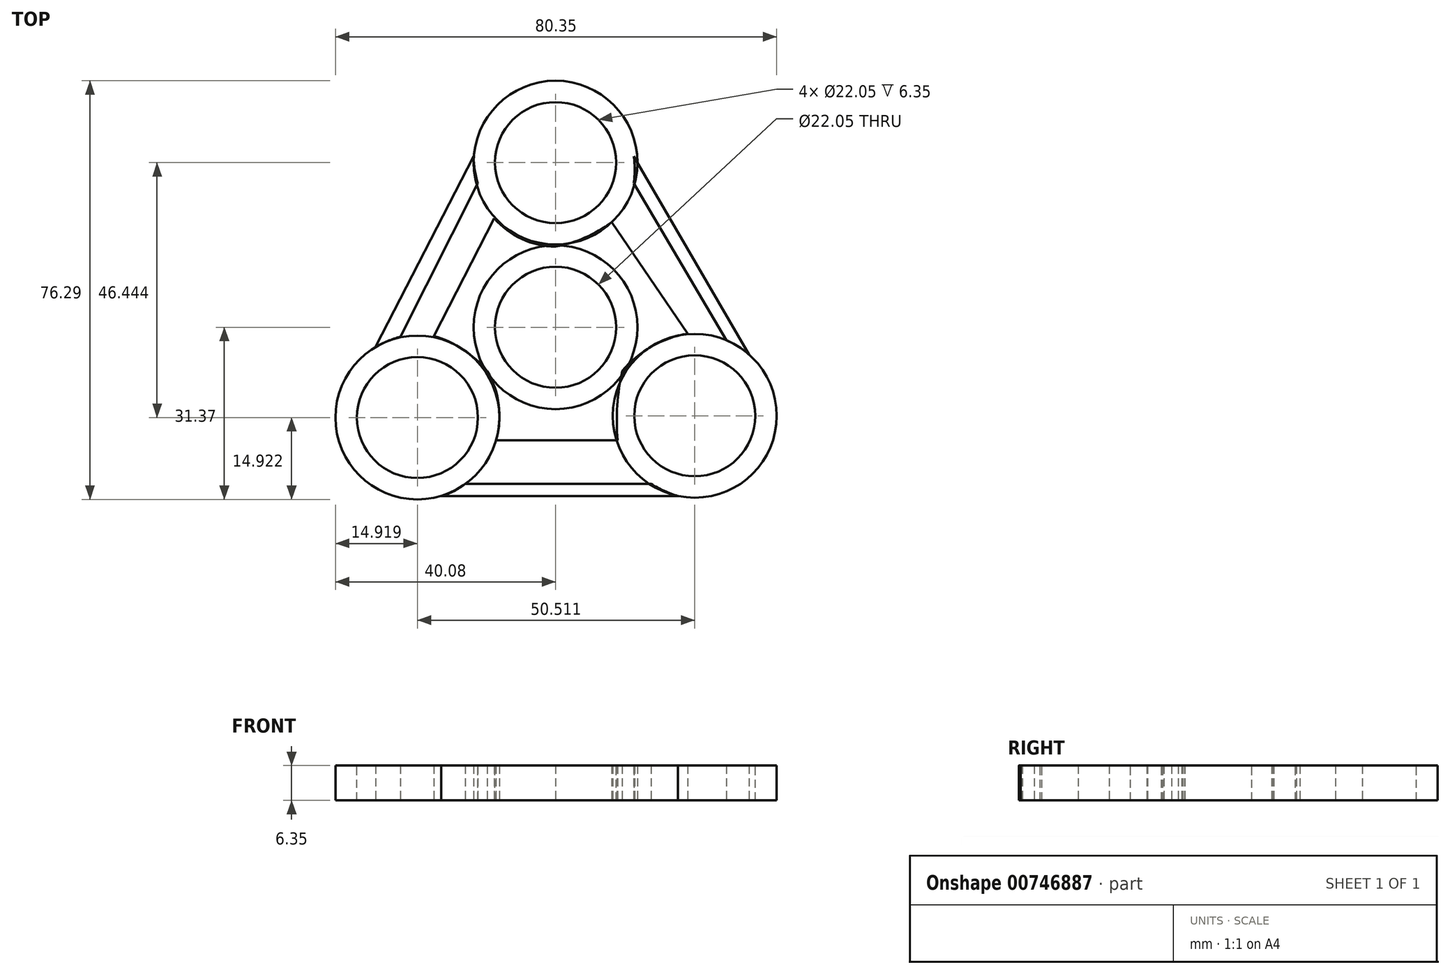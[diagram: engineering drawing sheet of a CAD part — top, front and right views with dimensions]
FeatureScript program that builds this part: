
annotation { "Feature Type Name" : "Feature", "Feature Type Description" : "" }
export const myFeature = defineFeature(function(context is Context, id is Id, definition is map)
    precondition{}
    {
        {
            var Q0;
            Q0=qCreatedBy(makeId("Top.planeOp"),FACE);
            var sketch = newSketch(context, id + "F0", { "sketchPlane" : qUnion([Q0])});
            skCircle(sketch, "E0", {"center": v(0, 0) * mm, "radius": 14.92 * mm});
            skSolve(sketch);
        }
        {
            var Q0;
            Q0 = qSketchRegion(id + "F0", true);
            extrude(context, id + "F1", {"entities" : qUnion([Q0]), "depth" : 6.35 * mm, "offsetDistance" : 25.4 * mm});
        }
        {
            var Q0;
            Q0=makeQuery(id+"F1.opExtrude","CAP_FACE",FACE,{"disambiguationData":[OSD([sQuery(id+"F0.wireOp",EDGE,"E0")])],"isStart":false});
            var sketch = newSketch(context, id + "F2", { "sketchPlane" : qUnion([Q0])});
            skCircle(sketch, "E1", {"center": v(0, 0) * mm, "radius": 11.02 * mm});
            skSolve(sketch);
        }
        {
            var Q0;
            Q0 = qSketchRegion(id + "F2", true);
            extrude(context, id + "F3", {"entities" : qUnion([Q0]), "operationType" : NewBodyOperationType.REMOVE, "oppositeDirection" : true, "depth" : 25.4 * mm, "offsetDistance" : 25.4 * mm});
        }
        {
            var Q0;
            Q0=qCreatedBy(makeId("Top.planeOp"),FACE);
            var sketch = newSketch(context, id + "F4", { "sketchPlane" : qUnion([Q0])});
            skCircle(sketch, "E2", {"center": v(0, 30) * mm, "radius": 14.92 * mm});
            skCircle(sketch, "E3", {"center": v(25.35, -16.14) * mm, "radius": 14.92 * mm});
            skCircle(sketch, "E4", {"center": v(-25.16, -16.45) * mm, "radius": 14.92 * mm});
            skSolve(sketch);
        }
        {
            var Q0;
            Q0 = qSketchRegion(id + "F4", true);
            extrude(context, id + "F5", {"entities" : qUnion([Q0]), "depth" : 6.35 * mm, "offsetDistance" : 25.4 * mm});
        }
        {
            var Q0;
            Q0=makeQuery(id+"F5.opExtrude","CAP_FACE",FACE,{"disambiguationData":[OSD([sQuery(id+"F4.wireOp",EDGE,"E2")])],"isStart":false});
            var sketch = newSketch(context, id + "F6", { "sketchPlane" : qUnion([Q0])});
            skCircle(sketch, "E5", {"center": v(-25.16, -16.45) * mm, "radius": 11.02 * mm});
            skSolve(sketch);
        }
        {
            var Q0;
            Q0 = qSketchRegion(id + "F6", true);
            extrude(context, id + "F7", {"entities" : qUnion([Q0]), "operationType" : NewBodyOperationType.REMOVE, "oppositeDirection" : true, "depth" : 25.4 * mm, "offsetDistance" : 25.4 * mm});
        }
        {
            var Q0;
            Q0=makeQuery(id+"F5.opExtrude","CAP_FACE",FACE,{"disambiguationData":[OSD([sQuery(id+"F4.wireOp",EDGE,"E3")])],"isStart":false});
            var sketch = newSketch(context, id + "F8", { "sketchPlane" : qUnion([Q0])});
            skCircle(sketch, "E6", {"center": v(25.35, -16.14) * mm, "radius": 11.02 * mm});
            skSolve(sketch);
        }
        {
            var Q0;
            Q0 = qSketchRegion(id + "F8", true);
            extrude(context, id + "F9", {"entities" : qUnion([Q0]), "operationType" : NewBodyOperationType.REMOVE, "oppositeDirection" : true, "depth" : 25.4 * mm, "offsetDistance" : 25.4 * mm});
        }
        {
            var Q0;
            Q0=makeQuery(id+"F5.opExtrude","CAP_FACE",FACE,{"disambiguationData":[OSD([sQuery(id+"F4.wireOp",EDGE,"E2")])],"isStart":false});
            var sketch = newSketch(context, id + "F10", { "sketchPlane" : qUnion([Q0])});
            skCircle(sketch, "E7", {"center": v(0, 30) * mm, "radius": 11.02 * mm});
            skSolve(sketch);
        }
        {
            var Q0;
            Q0 = qSketchRegion(id + "F10", true);
            extrude(context, id + "F11", {"entities" : qUnion([Q0]), "operationType" : NewBodyOperationType.REMOVE, "oppositeDirection" : true, "depth" : 25.4 * mm, "offsetDistance" : 25.4 * mm});
        }
        {
            var Q0;
            Q0=qCreatedBy(makeId("Top.planeOp"),FACE);
            var sketch = newSketch(context, id + "F12", { "sketchPlane" : qUnion([Q0])});
            skLineSegment(sketch, "E8", {"start": v(14.24, 26.27) * mm, "end": v(31.1, -2.37) * mm});
            skLineSegment(sketch, "E9", {"start": v(35.24, -4.98) * mm, "end": v(14.24, 31.17) * mm});
            skArc(sketch, "E10", {"start": v(14.24, 26.27) * mm, "mid": v(14.43, 28.72) * mm, "end": v(14.24, 31.17) * mm});
            skArc(sketch, "E11", {"start": v(35.24, -4.98) * mm, "mid": v(33.27, -3.5) * mm, "end": v(31.1, -2.37) * mm});
            skLineSegment(sketch, "E12", {"start": v(-20.8, -30.75) * mm, "end": v(22.32, -30.75) * mm});
            skLineSegment(sketch, "E13", {"start": v(17.42, -28.55) * mm, "end": v(-16.42, -28.55) * mm});
            skArc(sketch, "E14", {"start": v(-20.8, -30.75) * mm, "mid": v(-18.5, -29.86) * mm, "end": v(-16.42, -28.55) * mm});
            skArc(sketch, "E15", {"start": v(17.42, -28.55) * mm, "mid": v(19.8, -29.82) * mm, "end": v(22.32, -30.75) * mm});
            skLineSegment(sketch, "E16", {"start": v(-14.94, 31.17) * mm, "end": v(-32.78, -3.53) * mm});
            skLineSegment(sketch, "E17", {"start": v(-14.18, 26.27) * mm, "end": v(-28.23, -1.73) * mm});
            skArc(sketch, "E18", {"start": v(-14.94, 31.17) * mm, "mid": v(-14.74, 28.7) * mm, "end": v(-14.18, 26.27) * mm});
            skArc(sketch, "E19", {"start": v(-28.23, -1.73) * mm, "mid": v(-30.56, -2.5) * mm, "end": v(-32.78, -3.53) * mm});
            skSolve(sketch);
        }
        {
            var Q0;
            Q0=makeQuery(id+"F12.imprint","IMPRINT",FACE,{"disambiguationData":[TD([[makeQuery(id+"F12.imprint","IMPRINT",EDGE,{"derivedFrom":sQuery(id+"F12.wireOp",EDGE,"E16")}),1.0]])]});
            var Q1;
            Q1=makeQuery(id+"F12.imprint","IMPRINT",FACE,{"disambiguationData":[TD([[makeQuery(id+"F12.imprint","IMPRINT",EDGE,{"derivedFrom":sQuery(id+"F12.wireOp",EDGE,"E8")}),1.0]])]});
            var Q2;
            Q2=makeQuery(id+"F12.imprint","IMPRINT",FACE,{"disambiguationData":[TD([[makeQuery(id+"F12.imprint","IMPRINT",EDGE,{"derivedFrom":sQuery(id+"F12.wireOp",EDGE,"E12")}),1.0]])]});
            extrude(context, id + "F13", {"entities" : qUnion([Q0, Q1, Q2]), "depth" : 6.35 * mm, "offsetDistance" : 25.4 * mm});
        }
        {
            var Q0;
            Q0=qCreatedBy(makeId("Top.planeOp"),FACE);
            var sketch = newSketch(context, id + "F14", { "sketchPlane" : qUnion([Q0])});
            skLineSegment(sketch, "E20", {"start": v(10.2, 19.16) * mm, "end": v(24.08, -1.16) * mm});
            skArc(sketch, "E21", {"start": v(24.08, -1.16) * mm, "mid": v(17.52, -3.5) * mm, "end": v(12.16, -7.93) * mm});
            skArc(sketch, "E22", {"start": v(12.16, -7.93) * mm, "mid": v(12.76, 6.97) * mm, "end": v(0, 14.68) * mm});
            skArc(sketch, "E23", {"start": v(0, 14.68) * mm, "mid": v(5.36, 16.32) * mm, "end": v(10.2, 19.16) * mm});
            skLineSegment(sketch, "E24", {"start": v(-11.17, 19.83) * mm, "end": v(-22.15, -1.59) * mm});
            skArc(sketch, "E25", {"start": v(-11.17, 19.83) * mm, "mid": v(-6.14, 16.06) * mm, "end": v(0, 14.68) * mm});
            skArc(sketch, "E26", {"start": v(0, 14.68) * mm, "mid": v(-13.05, 7.06) * mm, "end": v(-12.42, -8.04) * mm});
            skArc(sketch, "E27", {"start": v(-12.42, -8.04) * mm, "mid": v(-16.8, -4.08) * mm, "end": v(-22.15, -1.59) * mm});
            skLineSegment(sketch, "E28", {"start": v(-10.84, -20.6) * mm, "end": v(11.32, -20.6) * mm});
            skArc(sketch, "E29", {"start": v(-10.84, -20.6) * mm, "mid": v(-10.34, -14.15) * mm, "end": v(-12.42, -8.04) * mm});
            skArc(sketch, "E30", {"start": v(-12.42, -8.04) * mm, "mid": v(-0.1, -14.82) * mm, "end": v(12.16, -7.93) * mm});
            skArc(sketch, "E31", {"start": v(12.16, -7.93) * mm, "mid": v(11.24, -14.23) * mm, "end": v(11.32, -20.6) * mm});
            skSolve(sketch);
        }
        {
            var Q0;
            Q0 = qSketchRegion(id + "F14", true);
            extrude(context, id + "F15", {"entities" : qUnion([Q0]), "depth" : 6.35 * mm, "offsetDistance" : 25.4 * mm});
        }
        {
            var Q0;
            Q0=makeQuery(id+"F15.opExtrude","CAP_FACE",FACE,{"disambiguationData":[OSD([sQuery(id+"F14.wireOp",EDGE,"E20"),sQuery(id+"F14.wireOp",EDGE,"E21"),sQuery(id+"F14.wireOp",EDGE,"E23"),sQuery(id+"F14.wireOp",EDGE,"E24"),sQuery(id+"F14.wireOp",EDGE,"E25"),sQuery(id+"F14.wireOp",EDGE,"E26"),sQuery(id+"F14.wireOp",EDGE,"E27"),sQuery(id+"F14.wireOp",EDGE,"E28"),sQuery(id+"F14.wireOp",EDGE,"E29"),sQuery(id+"F14.wireOp",EDGE,"E31")])],"isStart":false});
            var sketch = newSketch(context, id + "F16", { "sketchPlane" : qUnion([Q0])});
            skCircle(sketch, "E32", {"center": v(0, 0) * mm, "radius": 11.02 * mm});
            skSolve(sketch);
        }
        {
            var Q0;
            Q0 = qSketchRegion(id + "F16", true);
            extrude(context, id + "F17", {"entities" : qUnion([Q0]), "operationType" : NewBodyOperationType.REMOVE, "oppositeDirection" : true, "depth" : 25.4 * mm, "offsetDistance" : 25.4 * mm});
        }
    });
